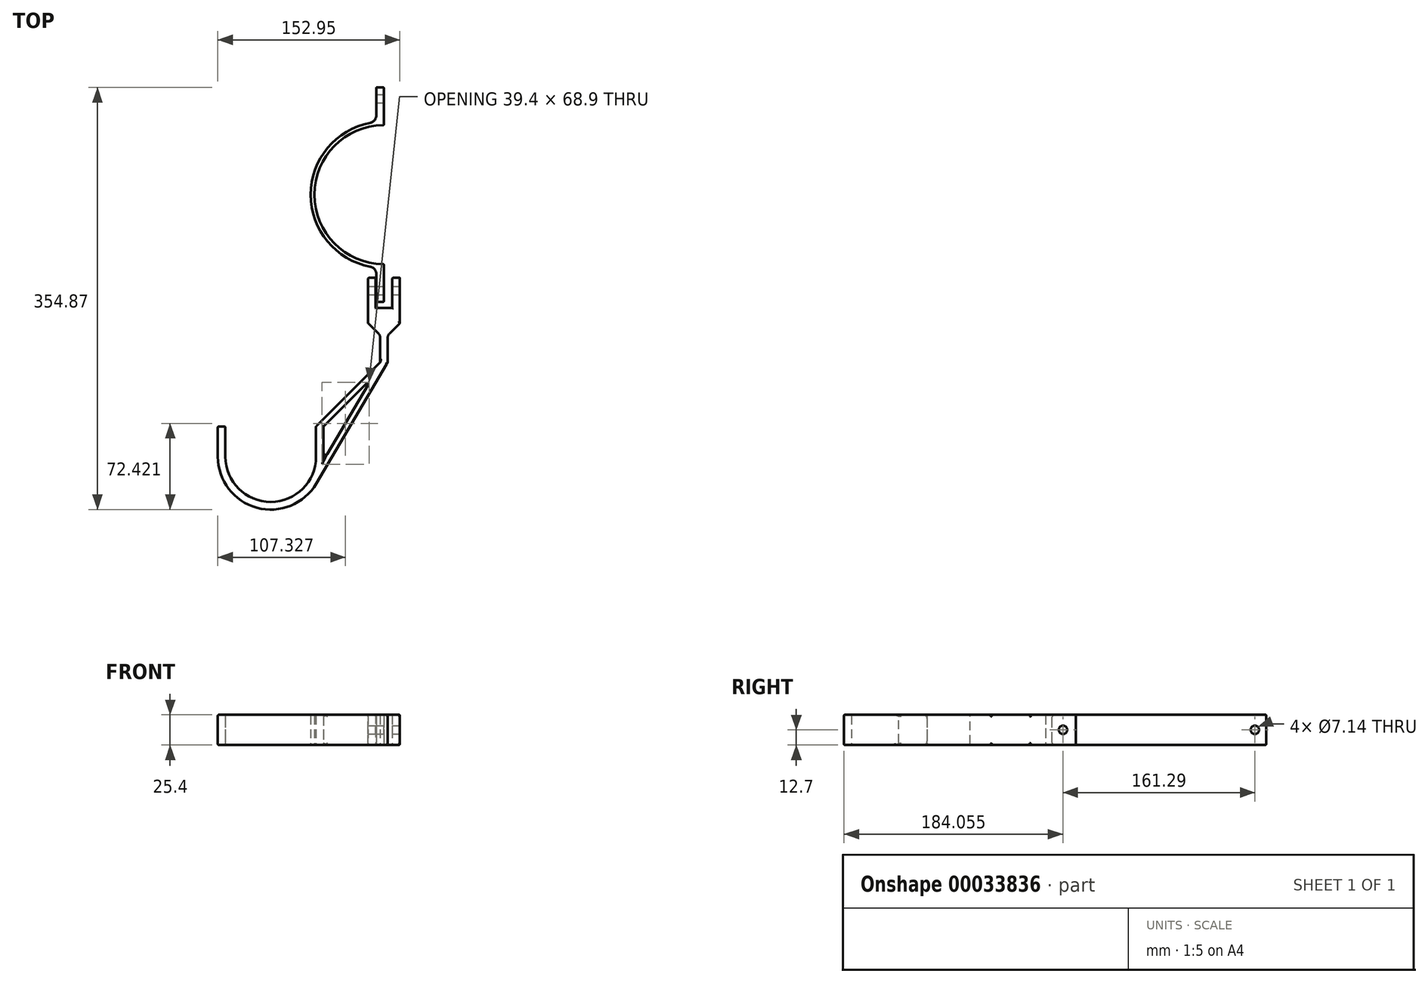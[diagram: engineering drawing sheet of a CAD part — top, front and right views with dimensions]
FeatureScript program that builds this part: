
annotation { "Feature Type Name" : "Feature", "Feature Type Description" : "" }
export const myFeature = defineFeature(function(context is Context, id is Id, definition is map)
    precondition{}
    {
        {
            var Q0;
            Q0=qCreatedBy(makeId("Top.planeOp"),FACE);
            var sketch = newSketch(context, id + "F0", { "sketchPlane" : qUnion([Q0])});
            skCircle(sketch, "E0", {"center": v(0, 0) * mm, "radius": 58.42 * mm, "construction": true});
            skCircle(sketch, "E1", {"center": v(0, 0) * mm, "radius": 61.6 * mm, "construction": true});
            skArc(sketch, "E2", {"start": v(0, 58.42) * mm, "mid": v(-58.42, 0) * mm, "end": v(0, -58.42) * mm});
            skArc(sketch, "E3", {"start": v(0, 61.6) * mm, "mid": v(-61.6, 0) * mm, "end": v(0, -61.6) * mm});
            skLineSegment(sketch, "E4.bottom", {"start": v(0, -58.42) * mm, "end": v(-6.35, -58.42) * mm});
            skLineSegment(sketch, "E4.top", {"start": v(0, -90.17) * mm, "end": v(-6.35, -90.17) * mm});
            skLineSegment(sketch, "E4.left", {"start": v(0, -58.42) * mm, "end": v(0, -90.17) * mm});
            skLineSegment(sketch, "E4.right", {"start": v(-6.35, -58.42) * mm, "end": v(-6.35, -90.17) * mm});
            skLineSegment(sketch, "E5.bottom", {"start": v(0, 58.42) * mm, "end": v(-6.35, 58.42) * mm});
            skLineSegment(sketch, "E5.top", {"start": v(0, 90.17) * mm, "end": v(-6.35, 90.17) * mm});
            skLineSegment(sketch, "E5.left", {"start": v(0, 58.42) * mm, "end": v(0, 90.17) * mm});
            skLineSegment(sketch, "E5.right", {"start": v(-6.35, 58.42) * mm, "end": v(-6.35, 90.17) * mm});
            skSolve(sketch);
        }
        {
            var Q0;
            Q0 = qSketchRegion(id + "F0", true);
            extrude(context, id + "F1", {"entities" : qUnion([Q0]), "depth" : 25.4 * mm, "offsetDistance" : 25.4 * mm});
        }
        {
            var Q0;
            Q0=makeQuery(id+"F1.opExtrude","SWEPT_EDGE",EDGE,{"disambiguationData":[OSD([sQuery(id+"F0.wireOp",EDGE,"E3"),sQuery(id+"F0.wireOp",EDGE,"E5.right")])]});
            var Q1;
            Q1=makeQuery(id+"F1.opExtrude","SWEPT_EDGE",EDGE,{"disambiguationData":[OSD([sQuery(id+"F0.wireOp",EDGE,"E3"),sQuery(id+"F0.wireOp",EDGE,"E4.right")])]});
            fillet(context, id + "F2", {"entities" : qUnion([Q0, Q1]), "radius" : 6.35 * mm, "tangentPropagation" : true, "allowEdgeOverflow" : false});
        }
        {
            var Q0;
            Q0=makeQuery(id+"F1.opExtrude","SWEPT_FACE",FACE,{"disambiguationData":[OSD([sQuery(id+"F0.wireOp",EDGE,"E4.left")])]});
            var sketch = newSketch(context, id + "F3", { "sketchPlane" : qUnion([Q0])});
            skPoint(sketch, "E6", {"position": v(-80.64, 12.7) * mm});
            skPoint(sketch, "E7", {"position": v(80.64, 12.7) * mm});
            skSolve(sketch);
        }
        {
            var Q0;
            Q0=sQuery(id+"F3.wireOp",VERTEX,"E6");
            var Q1;
            Q1=sQuery(id+"F3.wireOp",VERTEX,"E7");
            var Q2;
            Q2=makeQuery(id+"F1.opExtrude","SWEPT_BODY",BODY,{"disambiguationData":[OSD([sQuery(id+"F0.wireOp",EDGE,"E2"),sQuery(id+"F0.wireOp",EDGE,"E3"),sQuery(id+"F0.wireOp",EDGE,"E4.top"),sQuery(id+"F0.wireOp",EDGE,"E4.left"),sQuery(id+"F0.wireOp",EDGE,"E4.right"),sQuery(id+"F0.wireOp",EDGE,"E5.top"),sQuery(id+"F0.wireOp",EDGE,"E5.left"),sQuery(id+"F0.wireOp",EDGE,"E5.right")])]});
            hole(context, id + "F4", {"style" : HoleStyle.SIMPLE, "endStyle" : HoleEndStyle.THROUGH, "holeDiameter" : 7.14 * mm, "majorDiameter" : 6.35 * mm, "isTappedThrough" : true, "tappedDepth" : 19.94 * mm, "tapClearance" : 6, "startFromSketch" : true, "locations" : qUnion([Q0, Q1]), "scope" : qUnion([Q2])});
        }
        {
            var Q0;
            Q0=qCreatedBy(makeId("Top.planeOp"),FACE);
            var sketch = newSketch(context, id + "F5", { "sketchPlane" : qUnion([Q0])});
            skLineSegment(sketch, "E8", {"start": v(-6.99, -69.92) * mm, "end": v(-6.99, -95.32) * mm});
            skLineSegment(sketch, "E9", {"start": v(-6.99, -95.32) * mm, "end": v(6.99, -95.32) * mm});
            skLineSegment(sketch, "E10", {"start": v(6.99, -95.32) * mm, "end": v(6.99, -69.92) * mm});
            skLineSegment(sketch, "E11", {"start": v(6.99, -69.92) * mm, "end": v(13.33, -69.92) * mm});
            skLineSegment(sketch, "E12", {"start": v(13.33, -69.92) * mm, "end": v(13.34, -108.02) * mm});
            skLineSegment(sketch, "E13", {"start": v(-6.99, -69.92) * mm, "end": v(-13.34, -69.92) * mm});
            skLineSegment(sketch, "E14", {"start": v(-13.34, -69.92) * mm, "end": v(-13.34, -108.02) * mm});
            skLineSegment(sketch, "E15", {"start": v(-13.34, -108.02) * mm, "end": v(-3.17, -118.18) * mm});
            skLineSegment(sketch, "E16", {"start": v(-3.18, -118.18) * mm, "end": v(-3.18, -140.97) * mm});
            skLineSegment(sketch, "E17", {"start": v(13.34, -108.02) * mm, "end": v(3.18, -118.18) * mm});
            skLineSegment(sketch, "E18", {"start": v(3.18, -118.18) * mm, "end": v(3.18, -140.97) * mm});
            skArc(sketch, "E19", {"start": v(-133.26, -220.25) * mm, "mid": v(-95.16, -258.35) * mm, "end": v(-57.06, -220.25) * mm});
            skLineSegment(sketch, "E20", {"start": v(-133.26, -220.25) * mm, "end": v(-139.6, -220.25) * mm});
            skArc(sketch, "E21", {"start": v(-139.6, -220.25) * mm, "mid": v(-95.16, -264.7) * mm, "end": v(-50.7, -220.25) * mm});
            skLineSegment(sketch, "E22.bottom", {"start": v(-139.6, -220.25) * mm, "end": v(-133.26, -220.25) * mm});
            skLineSegment(sketch, "E22.top", {"start": v(-139.6, -194.85) * mm, "end": v(-133.26, -194.85) * mm});
            skLineSegment(sketch, "E22.left", {"start": v(-139.6, -220.25) * mm, "end": v(-139.6, -194.85) * mm});
            skLineSegment(sketch, "E22.right", {"start": v(-133.26, -220.25) * mm, "end": v(-133.26, -194.85) * mm});
            skLineSegment(sketch, "E23", {"start": v(3.18, -140.97) * mm, "end": v(-50.7, -194.85) * mm});
            skLineSegment(sketch, "E24", {"start": v(-3.17, -140.97) * mm, "end": v(-57.06, -194.85) * mm});
            skLineSegment(sketch, "E25", {"start": v(-139.6, -220.25) * mm, "end": v(-24.2, -220.25) * mm, "construction": true});
            skLineSegment(sketch, "E26", {"start": v(-57.06, -194.85) * mm, "end": v(-57.06, -220.25) * mm});
            skLineSegment(sketch, "E27", {"start": v(-50.7, -194.85) * mm, "end": v(-50.7, -220.25) * mm});
            skLineSegment(sketch, "E28", {"start": v(3.17, -140.97) * mm, "end": v(-56.86, -242.82) * mm});
            skLineSegment(sketch, "E29", {"start": v(-56.86, -242.82) * mm, "end": v(-50.8, -223.16) * mm});
            skLineSegment(sketch, "E30", {"start": v(-50.8, -223.16) * mm, "end": v(-10.3, -154.44) * mm});
            skSolve(sketch);
        }
        {
            var Q0;
            Q0 = qSketchRegion(id + "F5", true);
            extrude(context, id + "F6", {"entities" : qUnion([Q0]), "depth" : 25.4 * mm, "offsetDistance" : 25.4 * mm});
        }
        {
            var Q0;
            Q0=makeQuery(id+"F6.opExtrude","CAP_EDGE",EDGE,{"disambiguationData":[OSD([sQuery(id+"F5.wireOp",EDGE,"E22.top")])],"isStart":false});
            var Q1;
            Q1=makeQuery(id+"F6.opExtrude","CAP_EDGE",EDGE,{"disambiguationData":[OSD([sQuery(id+"F5.wireOp",EDGE,"E22.top")])],"isStart":true});
            fillet(context, id + "F7", {"entities" : qUnion([Q0, Q1]), "radius" : 3.17 * mm, "tangentPropagation" : true, "allowEdgeOverflow" : false});
        }
        {
            var Q0;
            Q0=makeQuery(id+"F6.opExtrude","SWEPT_EDGE",EDGE,{"disambiguationData":[OSD([sQuery(id+"F5.wireOp",EDGE,"E17"),sQuery(id+"F5.wireOp",EDGE,"E18")])]});
            var Q1;
            Q1=makeQuery(id+"F6.opExtrude","SWEPT_EDGE",EDGE,{"disambiguationData":[OSD([sQuery(id+"F5.wireOp",EDGE,"E15"),sQuery(id+"F5.wireOp",EDGE,"E16")])]});
            fillet(context, id + "F8", {"entities" : qUnion([Q0, Q1]), "radius" : 4.76 * mm, "tangentPropagation" : true, "allowEdgeOverflow" : false});
        }
        {
            var Q0;
            Q0=makeQuery(id+"F6.opExtrude","CAP_EDGE",EDGE,{"disambiguationData":[OSD([sQuery(id+"F5.wireOp",EDGE,"E16")])],"isStart":false});
            var Q1;
            Q1=makeQuery(id+"F6.opExtrude","CAP_EDGE",EDGE,{"disambiguationData":[OSD([sQuery(id+"F5.wireOp",EDGE,"E21")])],"isStart":false});
            var Q2;
            Q2=makeQuery(id+"F6.opExtrude","CAP_EDGE",EDGE,{"disambiguationData":[OSD([sQuery(id+"F5.wireOp",EDGE,"E14")])],"isStart":false});
            var Q3;
            Q3=makeQuery(id+"F6.opExtrude","CAP_EDGE",EDGE,{"disambiguationData":[OSD([sQuery(id+"F5.wireOp",EDGE,"E14")])],"isStart":true});
            var Q4;
            Q4=makeQuery(id+"F6.opExtrude","SWEPT_EDGE",EDGE,{"disambiguationData":[OSD([sQuery(id+"F5.wireOp",EDGE,"E14"),sQuery(id+"F5.wireOp",EDGE,"E15")])]});
            var Q5;
            Q5=makeQuery(id+"F6.opExtrude","SWEPT_EDGE",EDGE,{"disambiguationData":[OSD([sQuery(id+"F5.wireOp",EDGE,"E13"),sQuery(id+"F5.wireOp",EDGE,"E14")])]});
            var Q6;
            Q6=makeQuery(id+"F6.opExtrude","CAP_EDGE",EDGE,{"disambiguationData":[OSD([sQuery(id+"F5.wireOp",EDGE,"E12")])],"isStart":false});
            var Q7;
            Q7=makeQuery(id+"F6.opExtrude","CAP_EDGE",EDGE,{"disambiguationData":[OSD([sQuery(id+"F5.wireOp",EDGE,"E10")])],"isStart":false});
            var Q8;
            Q8=makeQuery(id+"F6.opExtrude","CAP_EDGE",EDGE,{"disambiguationData":[OSD([sQuery(id+"F5.wireOp",EDGE,"E12")])],"isStart":true});
            var Q9;
            Q9=makeQuery(id+"F6.opExtrude","CAP_EDGE",EDGE,{"disambiguationData":[OSD([sQuery(id+"F5.wireOp",EDGE,"E10")])],"isStart":true});
            var Q10;
            Q10=makeQuery(id+"F6.opExtrude","CAP_EDGE",EDGE,{"disambiguationData":[OSD([sQuery(id+"F5.wireOp",EDGE,"E11")])],"isStart":true});
            var Q11;
            Q11=makeQuery(id+"F6.opExtrude","CAP_EDGE",EDGE,{"disambiguationData":[OSD([sQuery(id+"F5.wireOp",EDGE,"E9")])],"isStart":true});
            var Q12;
            Q12=makeQuery(id+"F6.opExtrude","CAP_EDGE",EDGE,{"disambiguationData":[OSD([sQuery(id+"F5.wireOp",EDGE,"E13")])],"isStart":true});
            var Q13;
            Q13=makeQuery(id+"F6.opExtrude","CAP_EDGE",EDGE,{"disambiguationData":[OSD([sQuery(id+"F5.wireOp",EDGE,"E13")])],"isStart":false});
            var Q14;
            Q14=makeQuery(id+"F6.opExtrude","CAP_EDGE",EDGE,{"disambiguationData":[OSD([sQuery(id+"F5.wireOp",EDGE,"E11")])],"isStart":false});
            var Q15;
            Q15=makeQuery(id+"F6.opExtrude","CAP_EDGE",EDGE,{"disambiguationData":[OSD([sQuery(id+"F5.wireOp",EDGE,"E8")])],"isStart":true});
            var Q16;
            Q16=makeQuery(id+"F6.opExtrude","SWEPT_EDGE",EDGE,{"disambiguationData":[OSD([sQuery(id+"F5.wireOp",EDGE,"E10"),sQuery(id+"F5.wireOp",EDGE,"E11")])]});
            var Q17;
            Q17=makeQuery(id+"F6.opExtrude","SWEPT_EDGE",EDGE,{"disambiguationData":[OSD([sQuery(id+"F5.wireOp",EDGE,"E8"),sQuery(id+"F5.wireOp",EDGE,"E13")])]});
            fillet(context, id + "F9", {"entities" : qUnion([Q0, Q1, Q2, Q3, Q4, Q5, Q6, Q7, Q8, Q9, Q10, Q11, Q12, Q13, Q14, Q15, Q16, Q17]), "radius" : 0.8 * mm, "tangentPropagation" : true, "allowEdgeOverflow" : false});
        }
        {
            var Q0;
            Q0=makeQuery(id+"F6.opExtrude","SWEPT_FACE",FACE,{"disambiguationData":[OSD([sQuery(id+"F5.wireOp",EDGE,"E12")])]});
            var sketch = newSketch(context, id + "F10", { "sketchPlane" : qUnion([Q0])});
            skPoint(sketch, "E31", {"position": v(-80.64, 12.7) * mm});
            skPoint(sketch, "E31.positionSnap0", {"position": v(-88.97, 24.6) * mm});
            skSolve(sketch);
        }
        {
            var Q0;
            Q0=sQuery(id+"F10.wireOp",VERTEX,"E31");
            var Q1;
            Q1=makeQuery(id+"F1.opExtrude","SWEPT_BODY",BODY,{"disambiguationData":[OSD([sQuery(id+"F0.wireOp",EDGE,"E2"),sQuery(id+"F0.wireOp",EDGE,"E3"),sQuery(id+"F0.wireOp",EDGE,"E4.top"),sQuery(id+"F0.wireOp",EDGE,"E4.left"),sQuery(id+"F0.wireOp",EDGE,"E4.right"),sQuery(id+"F0.wireOp",EDGE,"E5.top"),sQuery(id+"F0.wireOp",EDGE,"E5.left"),sQuery(id+"F0.wireOp",EDGE,"E5.right")])]});
            var Q2;
            Q2=makeQuery(id+"F6.opExtrude","SWEPT_BODY",BODY,{"disambiguationData":[OSD([sQuery(id+"F5.wireOp",EDGE,"E8"),sQuery(id+"F5.wireOp",EDGE,"E9"),sQuery(id+"F5.wireOp",EDGE,"E10"),sQuery(id+"F5.wireOp",EDGE,"E11"),sQuery(id+"F5.wireOp",EDGE,"E12"),sQuery(id+"F5.wireOp",EDGE,"E13"),sQuery(id+"F5.wireOp",EDGE,"E14"),sQuery(id+"F5.wireOp",EDGE,"E15"),sQuery(id+"F5.wireOp",EDGE,"E16"),sQuery(id+"F5.wireOp",EDGE,"E17"),sQuery(id+"F5.wireOp",EDGE,"E18"),sQuery(id+"F5.wireOp",EDGE,"E19"),sQuery(id+"F5.wireOp",EDGE,"E21"),sQuery(id+"F5.wireOp",EDGE,"E22.top"),sQuery(id+"F5.wireOp",EDGE,"E22.left"),sQuery(id+"F5.wireOp",EDGE,"E22.right")])]});
            hole(context, id + "F11", {"style" : HoleStyle.SIMPLE, "endStyle" : HoleEndStyle.THROUGH, "holeDiameter" : 7.14 * mm, "majorDiameter" : 6.35 * mm, "isTappedThrough" : true, "tappedDepth" : 19.94 * mm, "tapClearance" : 6, "startFromSketch" : true, "locations" : qUnion([Q0]), "scope" : qUnion([Q1, Q2])});
        }
        {
            var Q0;
            Q0=makeQuery(id+"F1.opExtrude","CAP_EDGE",EDGE,{"disambiguationData":[OSD([sQuery(id+"F0.wireOp",EDGE,"E4.top")])],"isStart":true});
            var Q1;
            Q1=makeQuery(id+"F1.opExtrude","CAP_EDGE",EDGE,{"disambiguationData":[OSD([sQuery(id+"F0.wireOp",EDGE,"E4.top")])],"isStart":false});
            fillet(context, id + "F12", {"entities" : qUnion([Q0, Q1]), "radius" : 3.17 * mm, "tangentPropagation" : true, "allowEdgeOverflow" : false});
        }
        {
            var Q0;
            Q0=makeQuery(id+"F1.opExtrude","CAP_EDGE",EDGE,{"disambiguationData":[OSD([sQuery(id+"F0.wireOp",EDGE,"E2")])],"isStart":false});
            var Q1;
            Q1=makeQuery(id+"F1.opExtrude","CAP_EDGE",EDGE,{"disambiguationData":[OSD([sQuery(id+"F0.wireOp",EDGE,"E3")])],"isStart":false});
            var Q2;
            Q2=makeQuery(id+"F1.opExtrude","CAP_EDGE",EDGE,{"disambiguationData":[OSD([sQuery(id+"F0.wireOp",EDGE,"E4.left")])],"isStart":false});
            var Q3;
            Q3=makeQuery(id+"F1.opExtrude","CAP_EDGE",EDGE,{"disambiguationData":[OSD([sQuery(id+"F0.wireOp",EDGE,"E5.left")])],"isStart":false});
            var Q4;
            Q4=makeQuery(id+"F1.opExtrude","SWEPT_EDGE",EDGE,{"disambiguationData":[OSD([sQuery(id+"F0.wireOp",EDGE,"E5.top"),sQuery(id+"F0.wireOp",EDGE,"E5.left")])]});
            var Q5;
            Q5=makeQuery(id+"F1.opExtrude","CAP_EDGE",EDGE,{"disambiguationData":[OSD([sQuery(id+"F0.wireOp",EDGE,"E5.left")])],"isStart":true});
            var Q6;
            Q6=makeQuery(id+"F1.opExtrude","CAP_EDGE",EDGE,{"disambiguationData":[OSD([sQuery(id+"F0.wireOp",EDGE,"E5.top")])],"isStart":false});
            var Q7;
            Q7=makeQuery(id+"F1.opExtrude","CAP_EDGE",EDGE,{"disambiguationData":[OSD([sQuery(id+"F0.wireOp",EDGE,"E5.top")])],"isStart":true});
            var Q8;
            Q8=makeQuery(id+"F1.opExtrude","CAP_EDGE",EDGE,{"disambiguationData":[OSD([sQuery(id+"F0.wireOp",EDGE,"E2")])],"isStart":true});
            var Q9;
            Q9=makeQuery(id+"F1.opExtrude","SWEPT_EDGE",EDGE,{"disambiguationData":[OSD([sQuery(id+"F0.wireOp",EDGE,"E2"),sQuery(id+"F0.wireOp",EDGE,"E4.bottom"),sQuery(id+"F0.wireOp",EDGE,"E4.left")])]});
            var Q10;
            Q10=makeQuery(id+"F1.opExtrude","SWEPT_EDGE",EDGE,{"disambiguationData":[OSD([sQuery(id+"F0.wireOp",EDGE,"E2"),sQuery(id+"F0.wireOp",EDGE,"E5.bottom"),sQuery(id+"F0.wireOp",EDGE,"E5.left")])]});
            fillet(context, id + "F13", {"entities" : qUnion([Q0, Q1, Q2, Q3, Q4, Q5, Q6, Q7, Q8, Q9, Q10]), "radius" : 0.8 * mm, "tangentPropagation" : true, "allowEdgeOverflow" : false});
        }
        {
            var Q0;
            Q0=makeQuery(id+"F6.opExtrude","SWEPT_EDGE",EDGE,{"disambiguationData":[OSD([sQuery(id+"F5.wireOp",EDGE,"E18"),sQuery(id+"F5.wireOp",EDGE,"E23")])]});
            var Q1;
            Q1=makeQuery(id+"F6.opExtrude","SWEPT_EDGE",EDGE,{"disambiguationData":[OSD([sQuery(id+"F5.wireOp",EDGE,"E16"),sQuery(id+"F5.wireOp",EDGE,"E24")])]});
            fillet(context, id + "F14", {"entities" : qUnion([Q0, Q1]), "radius" : 1.59 * mm, "tangentPropagation" : true, "allowEdgeOverflow" : false});
        }
        {
            var Q0;
            Q0=makeQuery(id+"F6.opExtrude","SWEPT_EDGE",EDGE,{"disambiguationData":[OSD([sQuery(id+"F5.wireOp",EDGE,"E23"),sQuery(id+"F5.wireOp",EDGE,"E30")])]});
            var Q1;
            Q1=makeQuery(id+"F6.opExtrude","CAP_EDGE",EDGE,{"disambiguationData":[OSD([sQuery(id+"F5.wireOp",EDGE,"E23")])],"isStart":false});
            var Q2;
            Q2=makeQuery(id+"F6.opExtrude","CAP_EDGE",EDGE,{"disambiguationData":[OSD([sQuery(id+"F5.wireOp",EDGE,"E30")])],"isStart":false});
            var Q3;
            Q3=makeQuery(id+"F6.opExtrude","CAP_EDGE",EDGE,{"disambiguationData":[OSD([sQuery(id+"F5.wireOp",EDGE,"E27")])],"isStart":true});
            var Q4;
            Q4=makeQuery(id+"F6.opExtrude","CAP_EDGE",EDGE,{"disambiguationData":[OSD([sQuery(id+"F5.wireOp",EDGE,"E30")])],"isStart":true});
            var Q5;
            Q5=makeQuery(id+"F6.opExtrude","CAP_EDGE",EDGE,{"disambiguationData":[OSD([sQuery(id+"F5.wireOp",EDGE,"E23")])],"isStart":true});
            fillet(context, id + "F15", {"entities" : qUnion([Q0, Q1, Q2, Q3, Q4, Q5]), "radius" : 0.8 * mm, "allowEdgeOverflow" : false});
        }
        {
            var Q0;
            {var subQ0=sQuery(id+"F5.wireOp",EDGE,"E21");Q0=makeQuery(id+"F6.opExtrude","CAP_EDGE",EDGE,{"disambiguationData":[OSD([subQ0]),TDD([makeQuery(id+"F5.imprint","IMPRINT",EDGE,{"disambiguationData":[TD([[makeQuery(id+"F5.imprint","INTERSECT",VERTEX,{"derivedFrom":[subQ0,sQuery(id+"F5.wireOp",EDGE,"E27")]}),1.0]])],"derivedFrom":subQ0})])],"isStart":true});}
            fillet(context, id + "F16", {"entities" : qUnion([Q0]), "radius" : 0.8 * mm, "tangentPropagation" : true, "allowEdgeOverflow" : false});
        }
        {
            var Q0;
            Q0=makeQuery(id+"F6.opExtrude","CAP_EDGE",EDGE,{"disambiguationData":[OSD([sQuery(id+"F5.wireOp",EDGE,"E26")])],"isStart":true});
            var Q1;
            Q1=makeQuery(id+"F6.opExtrude","CAP_EDGE",EDGE,{"disambiguationData":[OSD([sQuery(id+"F5.wireOp",EDGE,"E26")])],"isStart":false});
            var Q2;
            Q2=makeQuery(id+"F6.opExtrude","SWEPT_EDGE",EDGE,{"disambiguationData":[OSD([sQuery(id+"F5.wireOp",EDGE,"E24"),sQuery(id+"F5.wireOp",EDGE,"E26")])]});
            var Q3;
            Q3=makeQuery(id+"F6.opExtrude","CAP_EDGE",EDGE,{"disambiguationData":[OSD([sQuery(id+"F5.wireOp",EDGE,"E19")])],"isStart":true});
            var Q4;
            Q4=makeQuery(id+"F6.opExtrude","CAP_EDGE",EDGE,{"disambiguationData":[OSD([sQuery(id+"F5.wireOp",EDGE,"E19")])],"isStart":false});
            var Q5;
            Q5=makeQuery(id+"F6.opExtrude","SWEPT_FACE",FACE,{"disambiguationData":[OSD([sQuery(id+"F5.wireOp",EDGE,"E22.left")])]});
            var Q6;
            Q6=makeQuery(id+"F6.opExtrude","SWEPT_FACE",FACE,{"disambiguationData":[OSD([sQuery(id+"F5.wireOp",EDGE,"E22.right")])]});
            fillet(context, id + "F17", {"entities" : qUnion([Q0, Q1, Q2, Q3, Q4, Q5, Q6]), "radius" : 0.8 * mm, "tangentPropagation" : true, "allowEdgeOverflow" : false});
        }
        {
            var Q0;
            Q0=makeQuery(id+"F6.opExtrude","SWEPT_EDGE",EDGE,{"disambiguationData":[OSD([sQuery(id+"F5.wireOp",EDGE,"E21"),sQuery(id+"F5.wireOp",EDGE,"E29"),sQuery(id+"F5.wireOp",EDGE,"E30")])]});
            fillet(context, id + "F18", {"entities" : qUnion([Q0]), "radius" : 1.59 * mm, "tangentPropagation" : true, "allowEdgeOverflow" : false});
        }
    });
